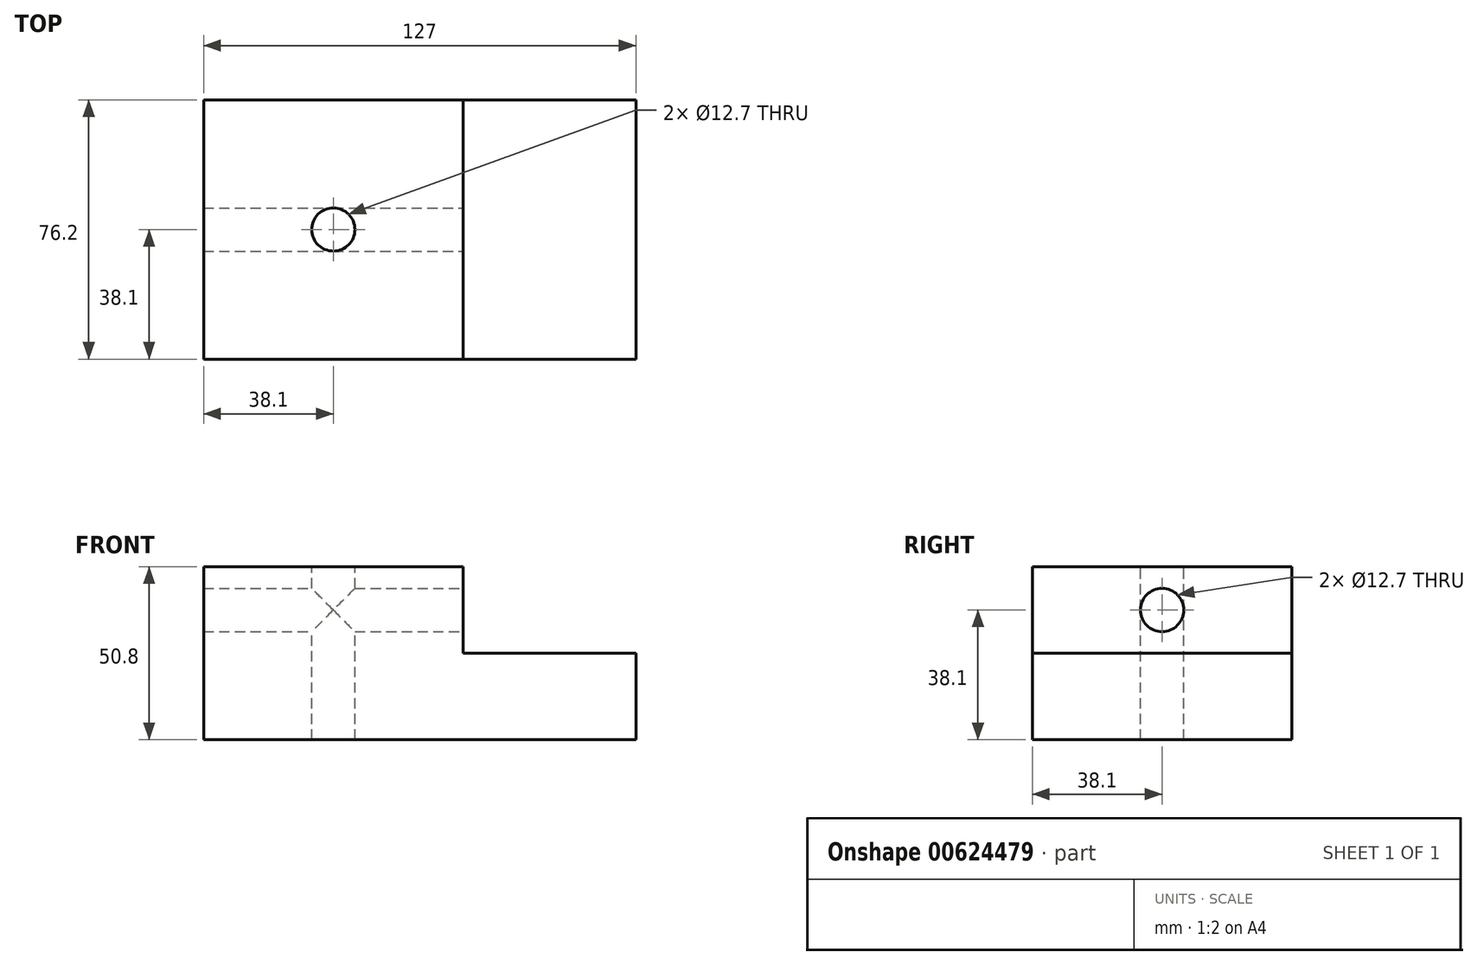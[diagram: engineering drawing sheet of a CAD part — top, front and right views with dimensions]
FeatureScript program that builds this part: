
annotation { "Feature Type Name" : "Feature", "Feature Type Description" : "" }
export const myFeature = defineFeature(function(context is Context, id is Id, definition is map)
    precondition{}
    {
        {
            var Q0;
            Q0=qCreatedBy(makeId("Front.planeOp"),FACE);
            var sketch = newSketch(context, id + "F0", { "sketchPlane" : qUnion([Q0])});
            skLineSegment(sketch, "E0.bottom", {"start": v(0, 0) * mm, "end": v(127, 0) * mm});
            skLineSegment(sketch, "E0.top", {"start": v(0, 50.8) * mm, "end": v(127, 50.8) * mm});
            skLineSegment(sketch, "E0.left", {"start": v(0, 0) * mm, "end": v(0, 50.8) * mm});
            skLineSegment(sketch, "E0.right", {"start": v(127, 0) * mm, "end": v(127, 50.8) * mm});
            skLineSegment(sketch, "E1", {"start": v(0, 50.8) * mm, "end": v(55.8, 50.8) * mm});
            skLineSegment(sketch, "E2", {"start": v(127, 25.4) * mm, "end": v(76.2, 25.4) * mm});
            skLineSegment(sketch, "E3", {"start": v(76.2, 25.4) * mm, "end": v(76.2, 50.8) * mm});
            skSolve(sketch);
        }
        {
            var Q0;
            {var subQ1=sQuery(id+"F0.wireOp",EDGE,"E0.bottom");Q0=makeQuery(id+"F0.imprint","IMPRINT",FACE,{"disambiguationData":[TD([[makeQuery(id+"F0.imprint","IMPRINT",EDGE,{"derivedFrom":subQ1}),1.0]])]});}
            extrude(context, id + "F1", {"entities" : qUnion([Q0]), "depth" : 76.2 * mm, "offsetDistance" : 25.4 * mm});
        }
        {
            var Q0;
            Q0=makeQuery(id+"F1.opExtrude","SWEPT_FACE",FACE,{"disambiguationData":[OSD([sQuery(id+"F0.wireOp",EDGE,"E0.top"),sQuery(id+"F0.wireOp",EDGE,"E1")])]});
            var sketch = newSketch(context, id + "F2", { "sketchPlane" : qUnion([Q0])});
            skLineSegment(sketch, "E4", {"start": v(38.1, -76.2) * mm, "end": v(38.1, -38.1) * mm});
            skLineSegment(sketch, "E5", {"start": v(38.1, -38.1) * mm, "end": v(0, -38.1) * mm});
            skSolve(sketch);
        }
        {
            var Q0;
            Q0=makeQuery(id+"F1.opExtrude","SWEPT_FACE",FACE,{"disambiguationData":[OSD([sQuery(id+"F0.wireOp",EDGE,"E3")])]});
            var sketch = newSketch(context, id + "F3", { "sketchPlane" : qUnion([Q0])});
            skLineSegment(sketch, "E6", {"start": v(-76.2, 38.1) * mm, "end": v(-38.1, 38.1) * mm});
            skLineSegment(sketch, "E7", {"start": v(-38.1, 38.1) * mm, "end": v(-38.1, 50.8) * mm});
            skSolve(sketch);
        }
        {
            var Q0;
            Q0=sQuery(id+"F2.wireOp",VERTEX,"E5.start");
            var Q1;
            Q1=makeQuery(id+"F1.opExtrude","SWEPT_BODY",BODY,{"disambiguationData":[OSD([sQuery(id+"F0.wireOp",EDGE,"E0.bottom"),sQuery(id+"F0.wireOp",EDGE,"E0.top"),sQuery(id+"F0.wireOp",EDGE,"E0.left"),sQuery(id+"F0.wireOp",EDGE,"E0.right"),sQuery(id+"F0.wireOp",EDGE,"E1"),sQuery(id+"F0.wireOp",EDGE,"E2"),sQuery(id+"F0.wireOp",EDGE,"E3")])]});
            hole(context, id + "F4", {"style" : HoleStyle.SIMPLE, "endStyle" : HoleEndStyle.THROUGH, "holeDiameter" : 12.7 * mm, "majorDiameter" : 6.35 * mm, "isTappedThrough" : true, "tappedDepth" : 12.7 * mm, "tapClearance" : 3, "locations" : qUnion([Q0]), "scope" : qUnion([Q1])});
        }
        {
            var Q0;
            Q0=sQuery(id+"F3.wireOp",VERTEX,"E7.start");
            var Q1;
            Q1=makeQuery(id+"F1.opExtrude","SWEPT_BODY",BODY,{"disambiguationData":[OSD([sQuery(id+"F0.wireOp",EDGE,"E0.bottom"),sQuery(id+"F0.wireOp",EDGE,"E0.top"),sQuery(id+"F0.wireOp",EDGE,"E0.left"),sQuery(id+"F0.wireOp",EDGE,"E0.right"),sQuery(id+"F0.wireOp",EDGE,"E1"),sQuery(id+"F0.wireOp",EDGE,"E2"),sQuery(id+"F0.wireOp",EDGE,"E3")])]});
            hole(context, id + "F5", {"style" : HoleStyle.SIMPLE, "endStyle" : HoleEndStyle.THROUGH, "holeDiameter" : 12.7 * mm, "majorDiameter" : 6.35 * mm, "isTappedThrough" : true, "tappedDepth" : 12.7 * mm, "tapClearance" : 3, "locations" : qUnion([Q0]), "scope" : qUnion([Q1])});
        }
    });
